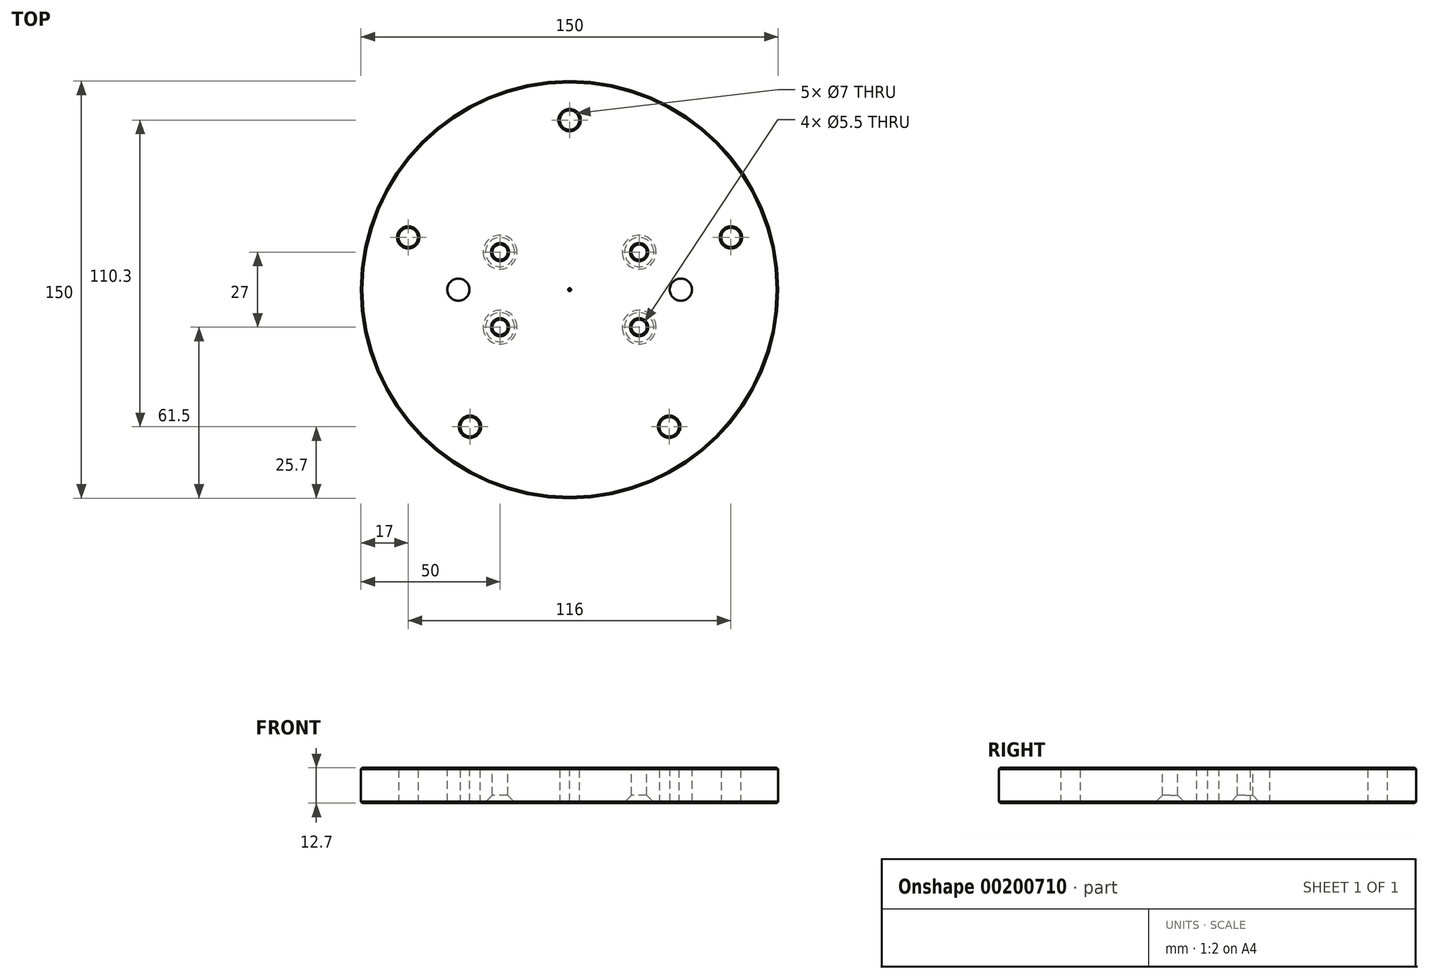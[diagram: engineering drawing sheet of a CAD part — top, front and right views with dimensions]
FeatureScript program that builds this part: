
annotation { "Feature Type Name" : "Feature", "Feature Type Description" : "" }
export const myFeature = defineFeature(function(context is Context, id is Id, definition is map)
    precondition{}
    {
        {
            var Q0;
            Q0=qCreatedBy(makeId("Top.planeOp"),FACE);
            var sketch = newSketch(context, id + "F0", { "sketchPlane" : qUnion([Q0])});
            skPoint(sketch, "E0.middle", {"position": v(0, 0) * mm});
            skCircle(sketch, "E1", {"center": v(0, 0) * mm, "radius": 75 * mm});
            skPoint(sketch, "E2", {"position": v(-25, 13.5) * mm});
            skPoint(sketch, "E3", {"position": v(25, 13.5) * mm});
            skPoint(sketch, "E4", {"position": v(25, -13.5) * mm});
            skPoint(sketch, "E5", {"position": v(-25, -13.5) * mm});
            skSolve(sketch);
        }
        {
            var Q0;
            Q0=makeQuery(id+"F0.imprint","IMPRINT",FACE,{"disambiguationData":[TD([[makeQuery(id+"F0.imprint","IMPRINT",EDGE,{"derivedFrom":sQuery(id+"F0.wireOp",EDGE,"E1")}),1.0]])]});
            extrude(context, id + "F1", {"entities" : qUnion([Q0]), "depth" : 12.7 * mm});
        }
        {
            var Q0;
            Q0=sQuery(id+"F0.wireOp",VERTEX,"E5");
            var Q1;
            Q1=sQuery(id+"F0.wireOp",VERTEX,"E4");
            var Q2;
            Q2=sQuery(id+"F0.wireOp",VERTEX,"E2");
            var Q3;
            Q3=sQuery(id+"F0.wireOp",VERTEX,"E3");
            var Q4;
            Q4=makeQuery(id+"F1.opExtrude","SWEPT_BODY",BODY,{"disambiguationData":[OSD([sQuery(id+"F0.wireOp",EDGE,"E1")])]});
            hole(context, id + "F2", {"style" : HoleStyle.C_SINK, "endStyle" : HoleEndStyle.THROUGH, "oppositeDirection" : true, "standardTappedOrClearance" : lookupTablePath({ "standard" : "ISO", "fit" : "Normal", "size" : "M5", "type" : "Clearance" }), "standardBlindInLast" : lookupTablePath({ "fit" : "Standard", "standard" : "ISO", "size" : "M5", "type" : "Clearance" }), "holeDiameter" : 5.5 * mm, "cSinkDiameter" : 11.2 * mm, "cSinkAngle" : 90 * degree, "locations" : qUnion([Q0, Q1, Q2, Q3]), "scope" : qUnion([Q4]), "isTappedThrough" : true, "startStyle" : HoleStartStyle.SKETCH});
        }
        {
            var Q0;
            Q0=makeQuery(id+"F1.opExtrude","CAP_FACE",FACE,{"disambiguationData":[OSD([sQuery(id+"F0.wireOp",EDGE,"E1")])],"isStart":false});
            var sketch = newSketch(context, id + "F3", { "sketchPlane" : qUnion([Q0])});
            skPoint(sketch, "E6", {"position": v(0, 61) * mm});
            skPoint(sketch, "E7", {"position": v(-58, 18.8) * mm});
            skPoint(sketch, "E8", {"position": v(58, 18.8) * mm});
            skPoint(sketch, "E9", {"position": v(-35.8, -49.3) * mm});
            skPoint(sketch, "E10", {"position": v(35.8, -49.3) * mm});
            skSolve(sketch);
        }
        {
            var Q0;
            Q0=sQuery(id+"F3.wireOp",VERTEX,"E6");
            var Q1;
            Q1=sQuery(id+"F3.wireOp",VERTEX,"E8");
            var Q2;
            Q2=sQuery(id+"F3.wireOp",VERTEX,"E7");
            var Q3;
            Q3=sQuery(id+"F3.wireOp",VERTEX,"E9");
            var Q4;
            Q4=sQuery(id+"F3.wireOp",VERTEX,"E10");
            var Q5;
            Q5=makeQuery(id+"F1.opExtrude","SWEPT_BODY",BODY,{"disambiguationData":[OSD([sQuery(id+"F0.wireOp",EDGE,"E1")])]});
            hole(context, id + "F4", {"style" : HoleStyle.SIMPLE, "endStyle" : HoleEndStyle.THROUGH, "standardTappedOrClearance" : lookupTablePath({ "standard" : "ISO", "engagement" : "75%", "pitch" : "1 mm", "size" : "M8", "type" : "Tapped" }), "standardBlindInLast" : lookupTablePath({ "standard" : "ISO", "engagement" : "75%", "pitch" : "1 mm", "size" : "M8", "type" : "Tapped" }), "holeDiameter" : 7 * mm, "locations" : qUnion([Q0, Q1, Q2, Q3, Q4]), "scope" : qUnion([Q5]), "isTappedThrough" : true, "majorDiameter" : 8 * mm, "showTappedDepth" : true, "startStyle" : HoleStartStyle.SKETCH});
        }
        {
            var Q0;
            Q0=sQuery(id+"F0.wireOp",VERTEX,"E0.middle");
            var Q1;
            Q1=makeQuery(id+"F1.opExtrude","SWEPT_BODY",BODY,{"disambiguationData":[OSD([sQuery(id+"F0.wireOp",EDGE,"E1")])]});
            hole(context, id + "F5", {"style" : HoleStyle.SIMPLE, "endStyle" : HoleEndStyle.THROUGH, "oppositeDirection" : true, "standardTappedOrClearance" : lookupTablePath({ "standard" : "ANSI", "size" : "5/16 (0.31)", "type" : "Drilled" }), "standardBlindInLast" : lookupTablePath({ "standard" : "ANSI", "size" : "5/16", "type" : "Drilled" }), "holeDiameter" : 5 / 406.4 * mm, "locations" : qUnion([Q0]), "scope" : qUnion([Q1]), "isTappedThrough" : true, "startStyle" : HoleStartStyle.SKETCH});
        }
        {
            var Q0;
            Q0=makeQuery(id+"F1.opExtrude","CAP_FACE",FACE,{"disambiguationData":[OSD([sQuery(id+"F0.wireOp",EDGE,"E1")])],"isStart":true});
            var Q1;
            Q1=makeQuery(id+"F1.opExtrude","CAP_FACE",FACE,{"disambiguationData":[OSD([sQuery(id+"F0.wireOp",EDGE,"E1")])],"isStart":false});
            chamfer(context, id + "F6", {"entities" : qUnion([Q0, Q1]), "width" : .5 * mm, "tangentPropagation" : true});
        }
        {
            var Q0;
            Q0=makeQuery(id+"F1.opExtrude","CAP_FACE",FACE,{"disambiguationData":[OSD([sQuery(id+"F0.wireOp",EDGE,"E1")])],"isStart":false});
            var sketch = newSketch(context, id + "F7", { "sketchPlane" : qUnion([Q0])});
            skPoint(sketch, "E11.0", {"position": v(-25, 13.5) * mm});
            skPoint(sketch, "E12.0", {"position": v(25, 13.5) * mm});
            skPoint(sketch, "E13", {"position": v(-40, 0) * mm});
            skPoint(sketch, "E14", {"position": v(40, 0) * mm});
            skSolve(sketch);
        }
        {
            var Q0;
            Q0=sQuery(id+"F7.wireOp",VERTEX,"E13");
            var Q1;
            Q1=sQuery(id+"F7.wireOp",VERTEX,"E14");
            var Q2;
            Q2=makeQuery(id+"F1.opExtrude","SWEPT_BODY",BODY,{"disambiguationData":[OSD([sQuery(id+"F0.wireOp",EDGE,"E1")])]});
            hole(context, id + "F8", {"style" : HoleStyle.SIMPLE, "endStyle" : HoleEndStyle.THROUGH, "standardTappedOrClearance" : lookupTablePath({ "standard" : "ISO", "size" : "8", "type" : "Drilled" }), "standardBlindInLast" : lookupTablePath({ "standard" : "ISO", "size" : "8", "type" : "Drilled" }), "holeDiameter" : 8 * mm, "locations" : qUnion([Q0, Q1]), "scope" : qUnion([Q2]), "isTappedThrough" : true, "startStyle" : HoleStartStyle.SKETCH});
        }
    });
